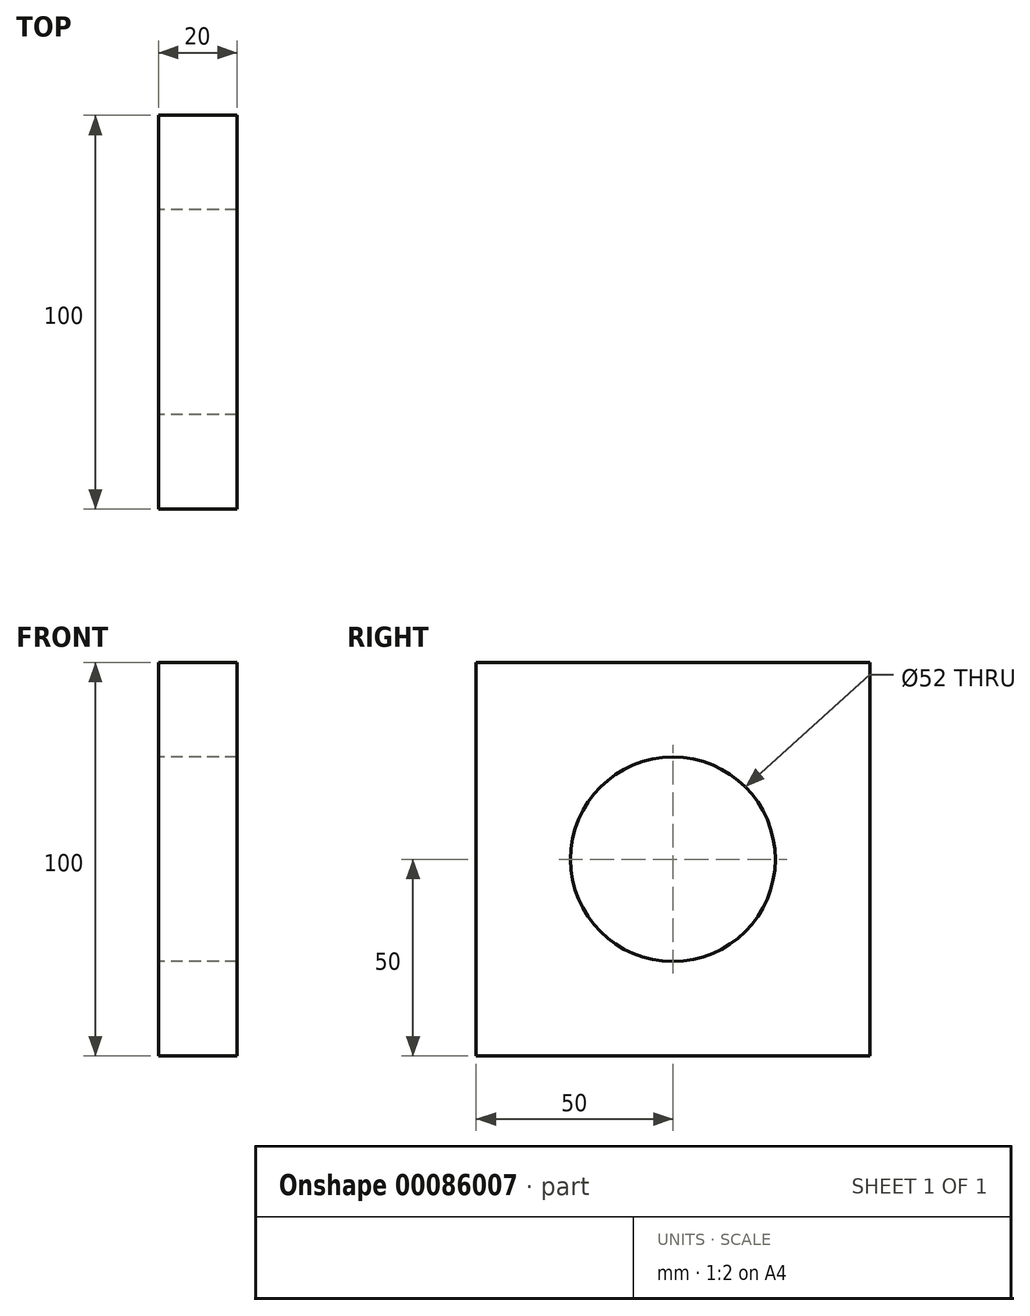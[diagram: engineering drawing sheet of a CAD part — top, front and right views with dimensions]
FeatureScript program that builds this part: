
annotation { "Feature Type Name" : "Feature", "Feature Type Description" : "" }
export const myFeature = defineFeature(function(context is Context, id is Id, definition is map)
    precondition{}
    {
        {
            var Q0;
            Q0=qCreatedBy(makeId("Right.planeOp"),FACE);
            var sketch = newSketch(context, id + "F0", { "sketchPlane" : qUnion([Q0])});
            skLineSegment(sketch, "E0.bottom", {"start": v(50, 50) * mm, "end": v(-50, 50) * mm});
            skLineSegment(sketch, "E0.top", {"start": v(50, -50) * mm, "end": v(-50, -50) * mm});
            skLineSegment(sketch, "E0.left", {"start": v(50, 50) * mm, "end": v(50, -50) * mm});
            skLineSegment(sketch, "E0.right", {"start": v(-50, 50) * mm, "end": v(-50, -50) * mm});
            skPoint(sketch, "E0.middle", {"position": v(0, 0) * mm});
            skCircle(sketch, "E1", {"center": v(0, 0) * mm, "radius": 26 * mm});
            skSolve(sketch);
        }
        {
            var Q0;
            Q0=makeQuery(id+"F0.imprint","IMPRINT",FACE,{"disambiguationData":[TD([[makeQuery(id+"F0.imprint","IMPRINT",EDGE,{"derivedFrom":sQuery(id+"F0.wireOp",EDGE,"E0.bottom")}),1.0]])]});
            extrude(context, id + "F1", {"entities" : qUnion([Q0]), "depth" : 20 * mm});
        }
    });
